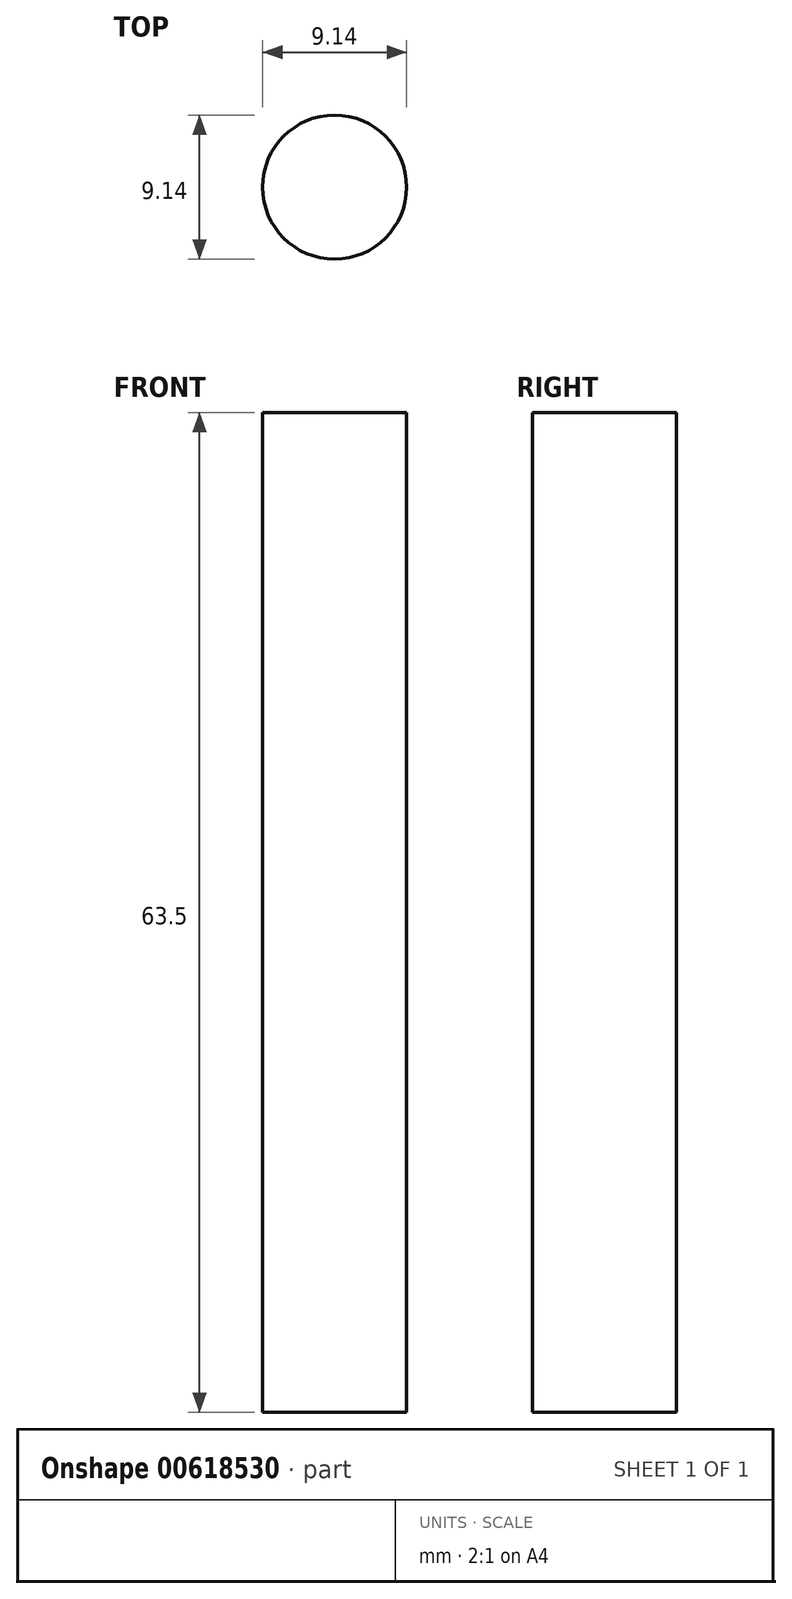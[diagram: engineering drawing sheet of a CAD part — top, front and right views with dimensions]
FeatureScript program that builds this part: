
annotation { "Feature Type Name" : "Feature", "Feature Type Description" : "" }
export const myFeature = defineFeature(function(context is Context, id is Id, definition is map)
    precondition{}
    {
        {
            var Q0;
            Q0=qCreatedBy(makeId("Top.planeOp"),FACE);
            var sketch = newSketch(context, id + "F0", { "sketchPlane" : qUnion([Q0])});
            skCircle(sketch, "E0", {"center": v(0, 0) * mm, "radius": 4.57 * mm});
            skSolve(sketch);
        }
        {
            var Q0;
            Q0=makeQuery(id+"F0.imprint","IMPRINT",FACE,{"disambiguationData":[TD([[makeQuery(id+"F0.imprint","IMPRINT",EDGE,{"derivedFrom":sQuery(id+"F0.wireOp",EDGE,"E0")}),1.0]])]});
            extrude(context, id + "F1", {"entities" : qUnion([Q0]), "depth" : 63.5 * mm, "offsetDistance" : 25.4 * mm});
        }
    });
